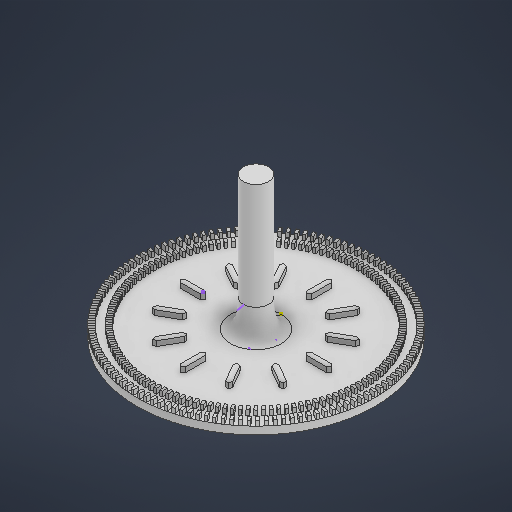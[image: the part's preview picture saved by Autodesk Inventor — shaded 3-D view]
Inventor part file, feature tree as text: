
AUTODESK INVENTOR PART (.ipt)
format: ipt  version: 2025 (Build 290162000, 162)  size: 4,344,320 bytes
history: native  units: mm
features: sketch x8, other x3, extrude x3, pattern_circular x2, revolve x1, projected_geometry x1
ambient origin geometry x8: Origin, YZ Plane, XZ Plane, XY Plane, X Axis, Y Axis, Z Axis, Center Point
bodies: Body1 (feature_tree)
feature tree (18):
  other  "Твердое тело1"
  revolve  "Вращение1"
  extrude  "Выдавливание1"  Depth=1.5mm
  pattern_circular  "Круговой массив1"  Angle=360.0deg  [1 undecoded]
  other  "РабПлоскость5"
  sketch  "Эскиз8"
  other  "РабПлоскость6"
  sketch  "Эскиз9"
  sketch  "Эскиз12"
  sketch  "Эскиз13"
  extrude  "Выдавливание3"  Depth=1.0mm
  pattern_circular  "Круговой массив3"  [2 undecoded]
  extrude  "Выдавливание4"  Depth=1.0mm TaperAngle=0.0deg
  sketch  "Эскиз1"
  sketch  "Эскиз2"
  projected_geometry  "Спроецированная петля2"
  sketch  "Эскиз15"
  sketch  "Эскиз16"
note: 3 required parameter values undecoded (feature->parameter linkage not recoverable at this tier; creation-order binding heuristic only, values carry confidence <= 0.55)
